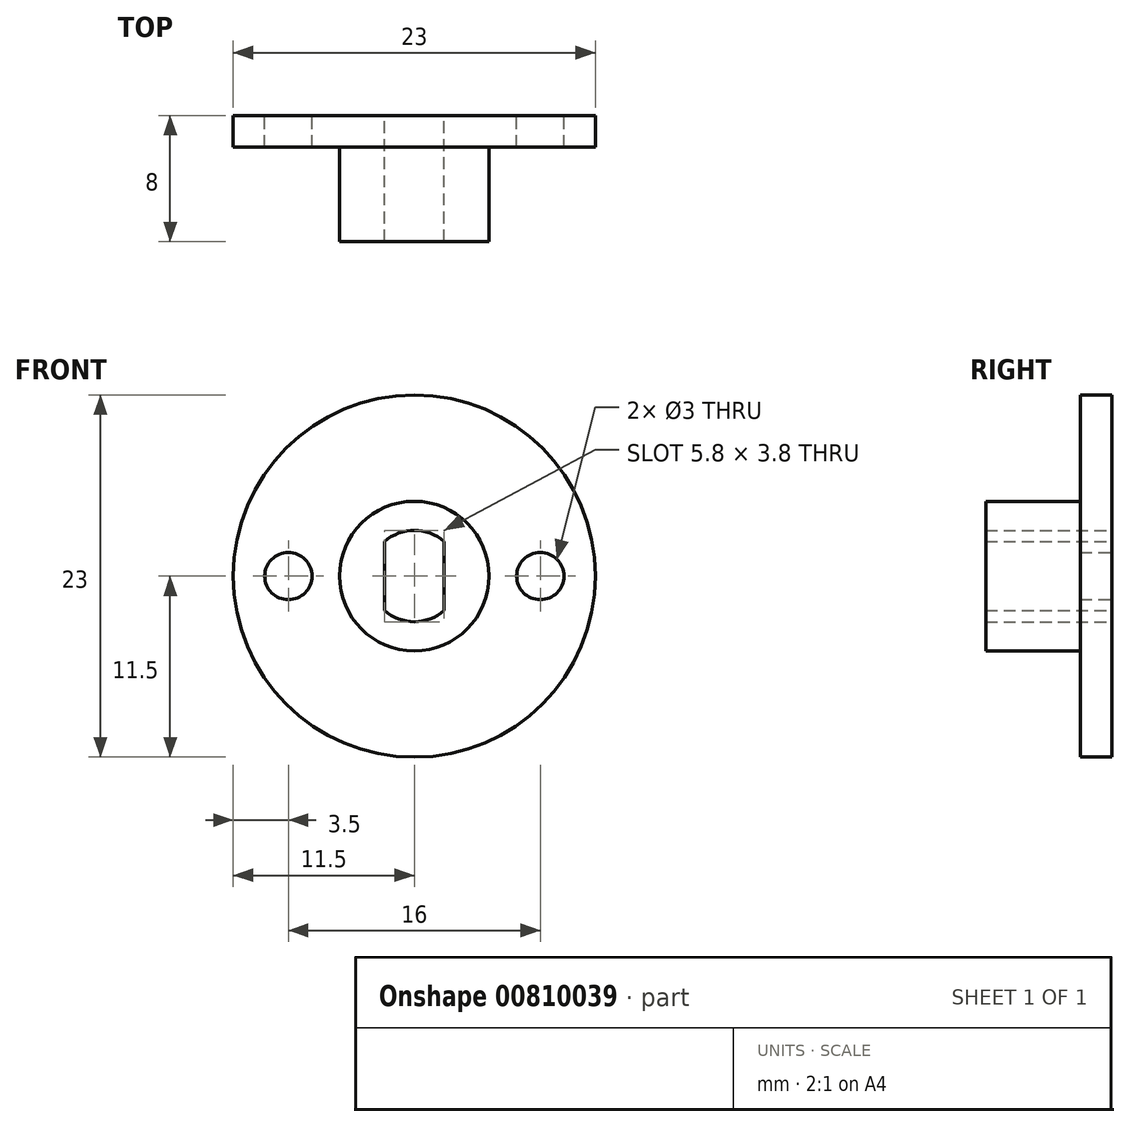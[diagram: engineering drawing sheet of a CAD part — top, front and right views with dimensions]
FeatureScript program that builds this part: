
annotation { "Feature Type Name" : "Feature", "Feature Type Description" : "" }
export const myFeature = defineFeature(function(context is Context, id is Id, definition is map)
    precondition{}
    {
        {
            var Q0;
            Q0=qCreatedBy(makeId("Front.planeOp"),FACE);
            var sketch = newSketch(context, id + "F0", { "sketchPlane" : qUnion([Q0])});
            skCircle(sketch, "E0", {"center": v(0, 0) * mm, "radius": 4.75 * mm});
            skCircle(sketch, "E1", {"center": v(0, 0) * mm, "radius": 2.9 * mm});
            skCircle(sketch, "E2", {"center": v(0, 0) * mm, "radius": 11.5 * mm});
            skCircle(sketch, "E3", {"center": v(-8, 0) * mm, "radius": 1.5 * mm});
            skCircle(sketch, "E4", {"center": v(8, 0) * mm, "radius": 1.5 * mm});
            skLineSegment(sketch, "E5", {"start": v(-8, 0) * mm, "end": v(0, 0) * mm, "construction": true});
            skLineSegment(sketch, "E6", {"start": v(0, 0) * mm, "end": v(8, 0) * mm, "construction": true});
            skLineSegment(sketch, "E7.bottom", {"start": v(1.9, 2.2) * mm, "end": v(-1.9, 2.2) * mm});
            skLineSegment(sketch, "E7.top", {"start": v(1.9, -2.2) * mm, "end": v(-1.9, -2.2) * mm});
            skLineSegment(sketch, "E7.left", {"start": v(1.9, 2.2) * mm, "end": v(1.9, -2.2) * mm});
            skLineSegment(sketch, "E7.right", {"start": v(-1.9, 2.2) * mm, "end": v(-1.9, -2.2) * mm});
            skSolve(sketch);
        }
        {
            var Q0;
            Q0=makeQuery(id+"F0.imprint","IMPRINT",FACE,{"disambiguationData":[TD([[makeQuery(id+"F0.imprint","IMPRINT",EDGE,{"derivedFrom":sQuery(id+"F0.wireOp",EDGE,"E0")}),1.0]])]});
            var Q1;
            {var subQ0=sQuery(id+"F0.wireOp",EDGE,"1e8cedca-056d-4308-bc52-5bcca275de9f");Q1=makeQuery(id+"F0.imprint","IMPRINT",FACE,{"disambiguationData":[TD([[makeQuery(id+"F0.imprint","IMPRINT",EDGE,{"derivedFrom":subQ0}),1.0]])]});}
            var Q2;
            {var subQ0=sQuery(id+"F0.wireOp",EDGE,"abda47cd-8e49-40fa-97a4-cba7a21ee996");Q2=makeQuery(id+"F0.imprint","IMPRINT",FACE,{"disambiguationData":[TD([[makeQuery(id+"F0.imprint","IMPRINT",EDGE,{"derivedFrom":subQ0}),1.0]])]});}
            var Q3;
            {var subQ0=sQuery(id+"F0.wireOp",EDGE,"E7.right");Q3=makeQuery(id+"F0.imprint","IMPRINT",FACE,{"disambiguationData":[TD([[makeQuery(id+"F0.imprint","IMPRINT",EDGE,{"derivedFrom":subQ0}),-1.0]])]});}
            var Q4;
            {var subQ0=sQuery(id+"F0.wireOp",EDGE,"E7.left");Q4=makeQuery(id+"F0.imprint","IMPRINT",FACE,{"disambiguationData":[TD([[makeQuery(id+"F0.imprint","IMPRINT",EDGE,{"derivedFrom":subQ0}),1.0]])]});}
            extrude(context, id + "F1", {"entities" : qUnion([Q0, Q1, Q2, Q3, Q4]), "depth" : 8 * mm, "offsetDistance" : 25 * mm});
        }
        {
            var Q0;
            Q0=qSketchRegion(id+"F0",true);
            extrude(context, id + "F2", {"entities" : qUnion([Q0]), "operationType" : NewBodyOperationType.ADD, "depth" : 2 * mm});
        }
    });
